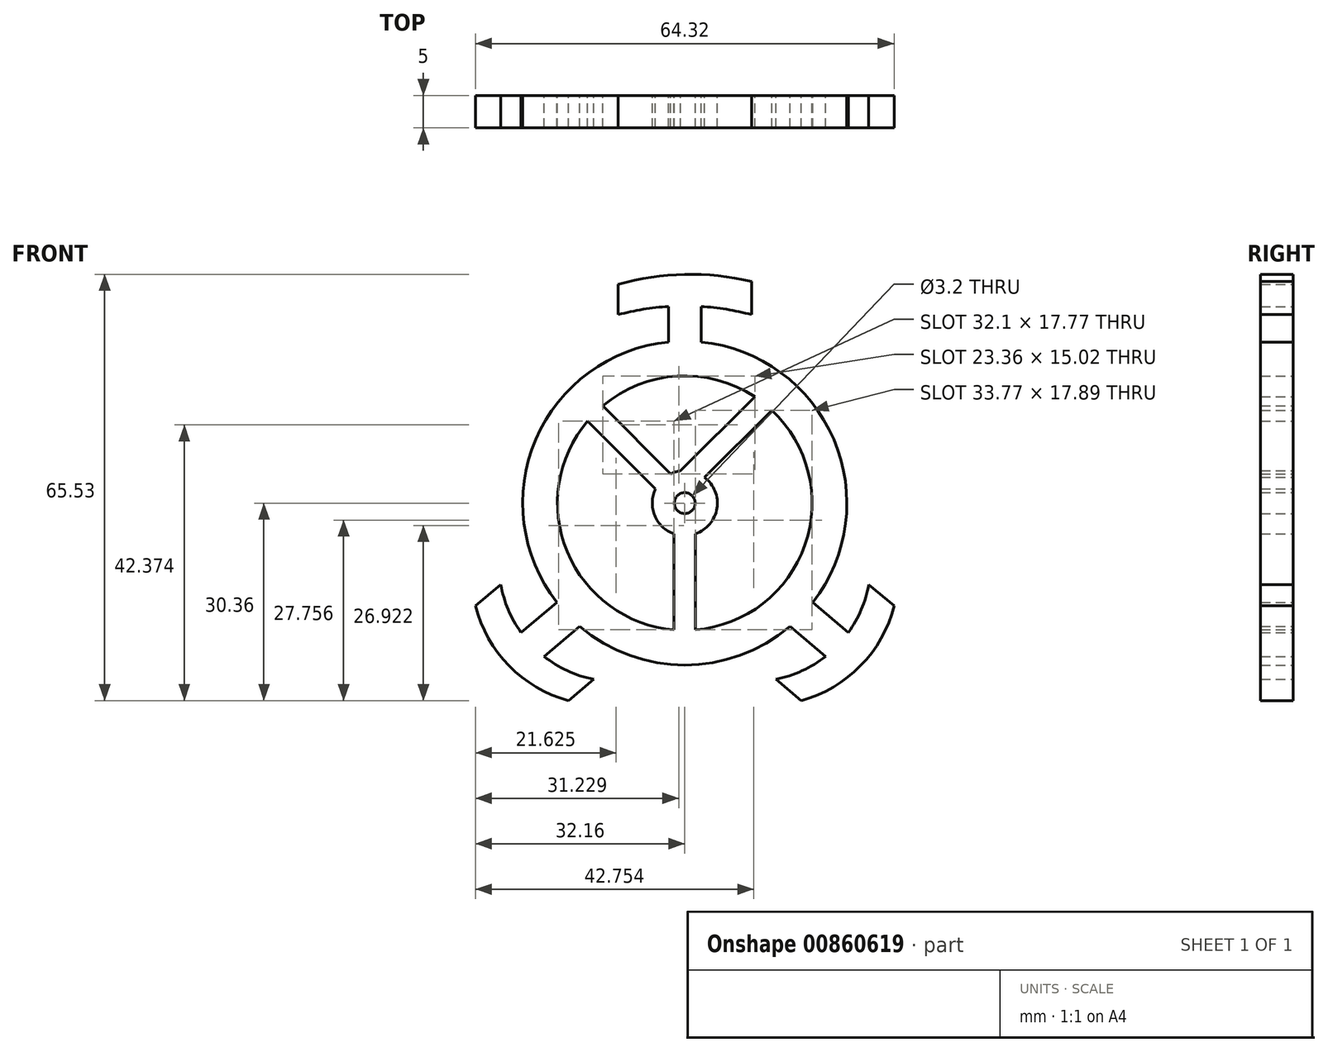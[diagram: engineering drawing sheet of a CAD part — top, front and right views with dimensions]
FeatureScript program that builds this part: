
annotation { "Feature Type Name" : "Feature", "Feature Type Description" : "" }
export const myFeature = defineFeature(function(context is Context, id is Id, definition is map)
    precondition{}
    {
        {
            var Q0;
            Q0=qCreatedBy(makeId("Front.planeOp"),FACE);
            var sketch = newSketch(context, id + "F0", { "sketchPlane" : qUnion([Q0])});
            skArc(sketch, "E0", {"start": v(-16.15, -18.94) * mm, "mid": v(0, -24.9) * mm, "end": v(16.15, -18.94) * mm});
            skArc(sketch, "E1", {"start": v(-14.95, 12.61) * mm, "mid": v(-18.07, -7.48) * mm, "end": v(-1.65, -19.49) * mm});
            skCircle(sketch, "E2", {"center": v(0, 0) * mm, "radius": 5 * mm});
            skLineSegment(sketch, "E3", {"start": v(-1.65, -4.72) * mm, "end": v(-1.65, -19.49) * mm});
            skLineSegment(sketch, "E4", {"start": v(1.65, -4.72) * mm, "end": v(1.65, -19.49) * mm});
            skLineSegment(sketch, "E5", {"start": v(-4.5, 2.17) * mm, "end": v(-14.95, 12.61) * mm});
            skLineSegment(sketch, "E6", {"start": v(-2.17, 4.5) * mm, "end": v(-12.61, 14.95) * mm});
            skLineSegment(sketch, "E7", {"start": v(-0.63, 4.96) * mm, "end": v(10.75, 16.34) * mm});
            skLineSegment(sketch, "E8", {"start": v(3.05, 3.96) * mm, "end": v(13.36, 14.28) * mm});
            skLineSegment(sketch, "E9", {"start": v(-16.15, -18.94) * mm, "end": v(-21.64, -23.56) * mm});
            skLineSegment(sketch, "E10", {"start": v(-28.27, -12.54) * mm, "end": v(-32.16, -15.8) * mm});
            skLineSegment(sketch, "E11", {"start": v(-14, -27.1) * mm, "end": v(-17.9, -30.36) * mm});
            skArc(sketch, "E12", {"start": v(-28.27, -12.54) * mm, "mid": v(-23.37, -22) * mm, "end": v(-14, -27.1) * mm});
            skLineSegment(sketch, "E13", {"start": v(-19.66, -15.26) * mm, "end": v(-25.16, -19.87) * mm});
            skArc(sketch, "E14", {"start": v(-32.16, -15.8) * mm, "mid": v(-27, -25.01) * mm, "end": v(-17.9, -30.36) * mm});
            skLineSegment(sketch, "E15.MirrorCS", {"start": v(28.27, -12.54) * mm, "end": v(32.16, -15.8) * mm});
            skArc(sketch, "E16.MirrorCS", {"start": v(28.27, -12.54) * mm, "mid": v(23.37, -22) * mm, "end": v(14, -27.1) * mm});
            skLineSegment(sketch, "E17.MirrorCS", {"start": v(16.15, -18.94) * mm, "end": v(21.64, -23.56) * mm});
            skArc(sketch, "E18.MirrorCS", {"start": v(32.16, -15.8) * mm, "mid": v(27, -25.01) * mm, "end": v(17.9, -30.36) * mm});
            skLineSegment(sketch, "E19.MirrorCS", {"start": v(19.66, -15.26) * mm, "end": v(25.16, -19.87) * mm});
            skLineSegment(sketch, "E20.MirrorCS", {"start": v(14, -27.1) * mm, "end": v(17.9, -30.36) * mm});
            skArc(sketch, "E21.trimOffspring", {"start": v(19.66, -15.26) * mm, "mid": v(22.88, 9.8) * mm, "end": v(2.5, 24.77) * mm});
            skLineSegment(sketch, "E22", {"start": v(-2.5, 24.77) * mm, "end": v(-2.5, 30.22) * mm});
            skLineSegment(sketch, "E23", {"start": v(10.24, 28.97) * mm, "end": v(10.24, 34.05) * mm});
            skLineSegment(sketch, "E24", {"start": v(-10.24, 28.97) * mm, "end": v(-10.24, 33.6) * mm});
            skArc(sketch, "E25", {"start": v(10.24, 28.97) * mm, "mid": v(0, 30.3) * mm, "end": v(-10.24, 28.97) * mm});
            skLineSegment(sketch, "E26", {"start": v(2.5, 24.77) * mm, "end": v(2.5, 30.22) * mm});
            skArc(sketch, "E27.trimOffspring", {"start": v(-2.5, 24.77) * mm, "mid": v(-22.88, 9.8) * mm, "end": v(-19.66, -15.26) * mm});
            skCircle(sketch, "E28", {"center": v(0, 0) * mm, "radius": 1.6 * mm});
            skArc(sketch, "E29.trimOffspring", {"start": v(10.75, 16.34) * mm, "mid": v(-1.16, 19.52) * mm, "end": v(-12.61, 14.95) * mm});
            skArc(sketch, "E30.trimOffspring", {"start": v(1.65, -19.49) * mm, "mid": v(18.48, -6.4) * mm, "end": v(13.36, 14.28) * mm});
            skArc(sketch, "E31", {"start": v(10.24, 34.05) * mm, "mid": v(-0.03, 35.16) * mm, "end": v(-10.24, 33.6) * mm});
            skSolve(sketch);
        }
        {
            var Q0;
            {var subQ3=sQuery(id+"F0.wireOp",EDGE,"E10");Q0=makeQuery(id+"F0.imprint","IMPRINT",FACE,{"disambiguationData":[TD([[makeQuery(id+"F0.imprint","IMPRINT",EDGE,{"derivedFrom":subQ3}),1.0]])]});}
            var Q1;
            {var subQ4=sQuery(id+"F0.wireOp",EDGE,"E15.MirrorCS");Q1=makeQuery(id+"F0.imprint","IMPRINT",FACE,{"disambiguationData":[TD([[makeQuery(id+"F0.imprint","IMPRINT",EDGE,{"derivedFrom":subQ4}),-1.0]])]});}
            var Q2;
            {var subQ3=sQuery(id+"F0.wireOp",EDGE,"E23");Q2=makeQuery(id+"F0.imprint","IMPRINT",FACE,{"disambiguationData":[TD([[makeQuery(id+"F0.imprint","IMPRINT",EDGE,{"derivedFrom":subQ3}),1.0]])]});}
            var Q3;
            Q3=makeQuery(id+"F0.imprint","IMPRINT",FACE,{"disambiguationData":[TD([[makeQuery(id+"F0.imprint","IMPRINT",EDGE,{"derivedFrom":sQuery(id+"F0.wireOp",EDGE,"E0")}),1.0]])]});
            var Q4;
            {var subQ0=sQuery(id+"F0.wireOp",EDGE,"E5");Q4=makeQuery(id+"F0.imprint","IMPRINT",FACE,{"disambiguationData":[TD([[makeQuery(id+"F0.imprint","IMPRINT",EDGE,{"derivedFrom":subQ0}),-1.0]])]});}
            var Q5;
            {var subQ0=sQuery(id+"F0.wireOp",EDGE,"E7");Q5=makeQuery(id+"F0.imprint","IMPRINT",FACE,{"disambiguationData":[TD([[makeQuery(id+"F0.imprint","IMPRINT",EDGE,{"derivedFrom":subQ0}),-1.0]])]});}
            var Q6;
            {var subQ0=sQuery(id+"F0.wireOp",EDGE,"E3");Q6=makeQuery(id+"F0.imprint","IMPRINT",FACE,{"disambiguationData":[TD([[makeQuery(id+"F0.imprint","IMPRINT",EDGE,{"derivedFrom":subQ0}),1.0]])]});}
            var Q7;
            Q7=makeQuery(id+"F0.imprint","IMPRINT",FACE,{"disambiguationData":[TD([[makeQuery(id+"F0.imprint","IMPRINT",EDGE,{"derivedFrom":sQuery(id+"F0.wireOp",EDGE,"E28")}),-1.0]])]});
            extrude(context, id + "F1", {"entities" : qUnion([Q0, Q1, Q2, Q3, Q4, Q5, Q6, Q7]), "depth" : 5 * mm, "offsetDistance" : 25.4 * mm});
        }
    });
